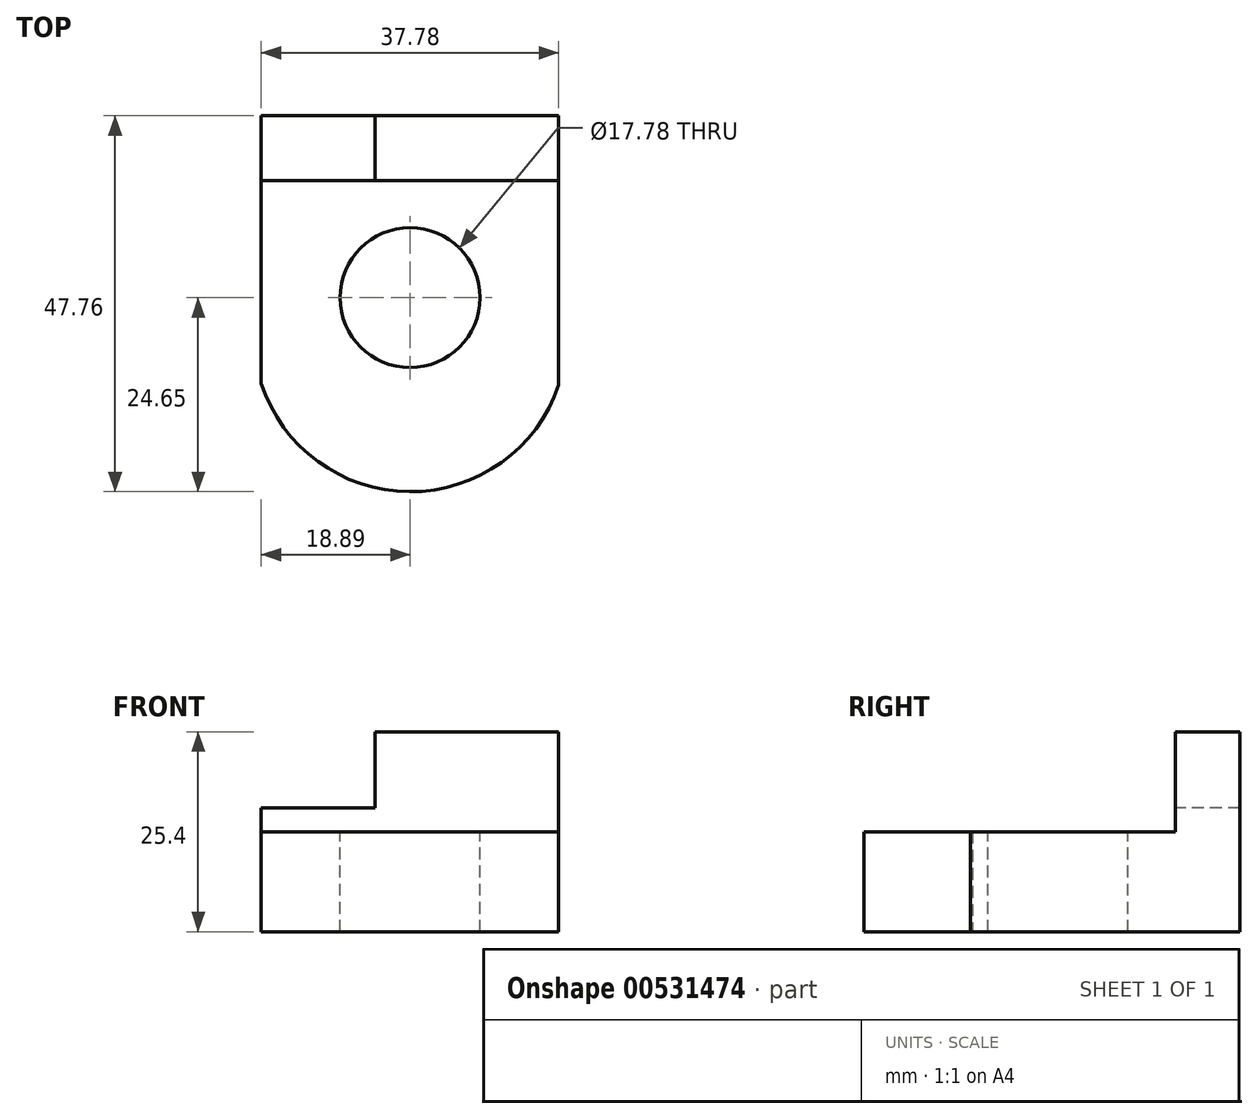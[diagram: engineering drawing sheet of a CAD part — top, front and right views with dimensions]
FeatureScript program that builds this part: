
annotation { "Feature Type Name" : "Feature", "Feature Type Description" : "" }
export const myFeature = defineFeature(function(context is Context, id is Id, definition is map)
    precondition{}
    {
        {
            var Q0;
            Q0=qCreatedBy(makeId("Top.planeOp"),FACE);
            var sketch = newSketch(context, id + "F0", { "sketchPlane" : qUnion([Q0])});
            skLineSegment(sketch, "E0.top", {"start": v(18.9, 23.11) * mm, "end": v(-18.9, 23.11) * mm});
            skLineSegment(sketch, "E0.left", {"start": v(18.9, -11.11) * mm, "end": v(18.9, 23.11) * mm});
            skLineSegment(sketch, "E0.right", {"start": v(-18.9, -10.9) * mm, "end": v(-18.9, 23.11) * mm});
            skPoint(sketch, "E0.middle", {"position": v(0, -2.67) * mm});
            skArc(sketch, "E1", {"start": v(-18.9, -10.9) * mm, "mid": v(-0.08, -24.65) * mm, "end": v(18.9, -11.11) * mm});
            skPoint(sketch, "E2.orphan", {"position": v(-18.9, -28.45) * mm});
            skPoint(sketch, "E3.orphan", {"position": v(18.9, -28.45) * mm});
            skSolve(sketch);
        }
        {
            var Q0;
            Q0=makeQuery(id+"F0.imprint","IMPRINT",FACE,{"disambiguationData":[TD([[makeQuery(id+"F0.imprint","IMPRINT",EDGE,{"derivedFrom":sQuery(id+"F0.wireOp",EDGE,"E0.top")}),1.0]])]});
            extrude(context, id + "F1", {"entities" : qUnion([Q0]), "depth" : 12.7 * mm, "offsetDistance" : 25.4 * mm});
        }
        {
            var Q0;
            Q0=makeQuery(id+"F1.opExtrude","CAP_FACE",FACE,{"disambiguationData":[OSD([sQuery(id+"F0.wireOp",EDGE,"E0.top"),sQuery(id+"F0.wireOp",EDGE,"E0.left"),sQuery(id+"F0.wireOp",EDGE,"E0.right"),sQuery(id+"F0.wireOp",EDGE,"E1")])],"isStart":false});
            var sketch = newSketch(context, id + "F2", { "sketchPlane" : qUnion([Q0])});
            skLineSegment(sketch, "E4.bottom", {"start": v(-18.9, 23.11) * mm, "end": v(18.9, 23.11) * mm});
            skLineSegment(sketch, "E4.top", {"start": v(-18.9, 14.9) * mm, "end": v(18.9, 14.9) * mm});
            skLineSegment(sketch, "E4.left", {"start": v(-18.9, 23.11) * mm, "end": v(-18.9, 14.9) * mm});
            skLineSegment(sketch, "E4.right", {"start": v(18.9, 23.11) * mm, "end": v(18.9, 14.9) * mm});
            skSolve(sketch);
        }
        {
            var Q0;
            Q0=makeQuery(id+"F2.imprint","IMPRINT",FACE,{"disambiguationData":[TD([[makeQuery(id+"F2.imprint","IMPRINT",EDGE,{"derivedFrom":sQuery(id+"F2.wireOp",EDGE,"E4.bottom")}),1.0]])]});
            extrude(context, id + "F3", {"entities" : qUnion([Q0]), "operationType" : NewBodyOperationType.ADD, "depth" : 12.7 * mm, "offsetDistance" : 25.4 * mm});
        }
        {
            var Q0;
            Q0=makeQuery(id+"F3.opExtrude","SWEPT_FACE",FACE,{"disambiguationData":[OSD([sQuery(id+"F2.wireOp",EDGE,"E4.top")])]});
            var sketch = newSketch(context, id + "F4", { "sketchPlane" : qUnion([Q0])});
            skLineSegment(sketch, "E5.bottom", {"start": v(-18.9, 25.4) * mm, "end": v(-4.43, 25.4) * mm});
            skLineSegment(sketch, "E5.top", {"start": v(-18.9, 15.71) * mm, "end": v(-4.43, 15.71) * mm});
            skLineSegment(sketch, "E5.left", {"start": v(-18.9, 25.4) * mm, "end": v(-18.9, 15.71) * mm});
            skLineSegment(sketch, "E5.right", {"start": v(-4.43, 25.4) * mm, "end": v(-4.43, 15.71) * mm});
            skSolve(sketch);
        }
        {
            var Q0;
            Q0=makeQuery(id+"F4.imprint","IMPRINT",FACE,{"disambiguationData":[TD([[makeQuery(id+"F4.imprint","IMPRINT",EDGE,{"derivedFrom":sQuery(id+"F4.wireOp",EDGE,"E5.bottom")}),-1.0]])]});
            extrude(context, id + "F5", {"entities" : qUnion([Q0]), "operationType" : NewBodyOperationType.REMOVE, "endBound" : BoundingType.THROUGH_ALL, "oppositeDirection" : true, "depth" : 25.4 * mm, "offsetDistance" : 25.4 * mm});
        }
        {
            var Q0;
            Q0=makeQuery(id+"F1.opExtrude","CAP_FACE",FACE,{"disambiguationData":[OSD([sQuery(id+"F0.wireOp",EDGE,"E0.top"),sQuery(id+"F0.wireOp",EDGE,"E0.left"),sQuery(id+"F0.wireOp",EDGE,"E0.right"),sQuery(id+"F0.wireOp",EDGE,"E1")])],"isStart":false});
            var sketch = newSketch(context, id + "F6", { "sketchPlane" : qUnion([Q0])});
            skCircle(sketch, "E6", {"center": v(0, 0) * mm, "radius": 8.9 * mm});
            skSolve(sketch);
        }
        {
            var Q0;
            Q0=makeQuery(id+"F6.imprint","IMPRINT",FACE,{"disambiguationData":[TD([[makeQuery(id+"F6.imprint","IMPRINT",EDGE,{"derivedFrom":sQuery(id+"F6.wireOp",EDGE,"E6")}),1.0]])]});
            extrude(context, id + "F7", {"entities" : qUnion([Q0]), "operationType" : NewBodyOperationType.REMOVE, "endBound" : BoundingType.THROUGH_ALL, "oppositeDirection" : true, "depth" : 16.5 * mm, "offsetDistance" : 25.4 * mm});
        }
    });
